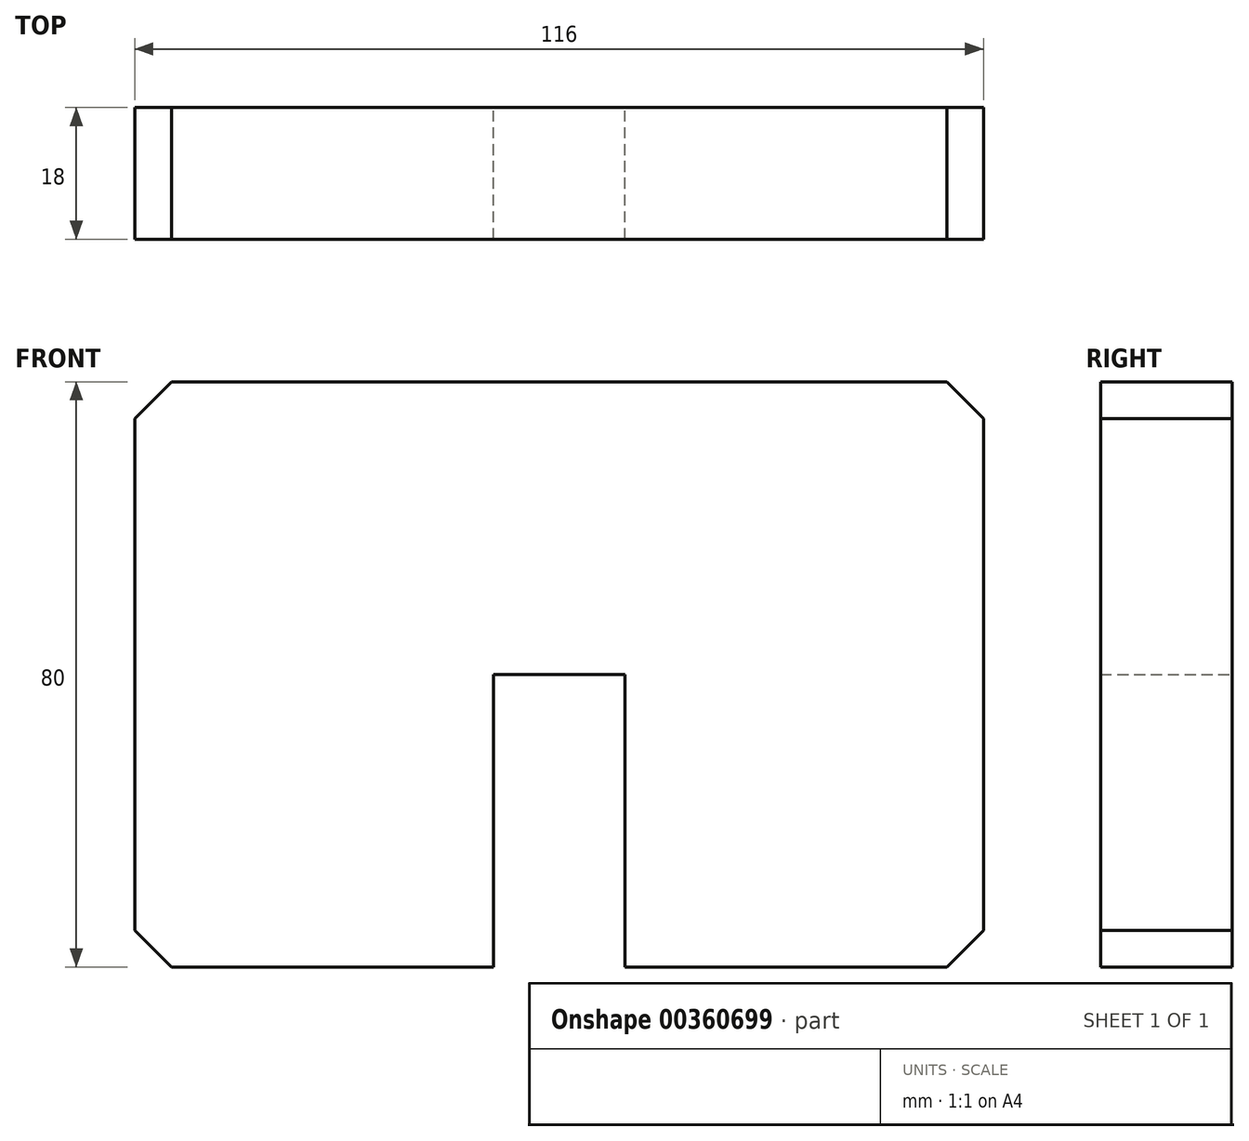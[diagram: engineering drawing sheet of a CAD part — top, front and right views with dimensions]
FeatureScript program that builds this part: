
annotation { "Feature Type Name" : "Feature", "Feature Type Description" : "" }
export const myFeature = defineFeature(function(context is Context, id is Id, definition is map)
    precondition{}
    {
        {
            var Q0;
            Q0=qCreatedBy(makeId("Front.planeOp"),FACE);
            var sketch = newSketch(context, id + "F0", { "sketchPlane" : qUnion([Q0])});
            skLineSegment(sketch, "E0.bottom", {"start": v(-58, 0) * mm, "end": v(-9, 0) * mm});
            skLineSegment(sketch, "E0.top", {"start": v(-58, 80) * mm, "end": v(58, 80) * mm});
            skLineSegment(sketch, "E0.left", {"start": v(-58, 0) * mm, "end": v(-58, 80) * mm});
            skLineSegment(sketch, "E0.right", {"start": v(58, 0) * mm, "end": v(58, 80) * mm});
            skLineSegment(sketch, "E1.top", {"start": v(-9, 40) * mm, "end": v(9, 40) * mm});
            skLineSegment(sketch, "E1.left", {"start": v(-9, 0) * mm, "end": v(-9, 40) * mm});
            skLineSegment(sketch, "E1.right", {"start": v(9, 0) * mm, "end": v(9, 40) * mm});
            skLineSegment(sketch, "E2.trimOffspring", {"start": v(9, 0) * mm, "end": v(58, 0) * mm});
            skSolve(sketch);
        }
        {
            var Q0;
            Q0=makeQuery(id+"F0.imprint","IMPRINT",FACE,{"disambiguationData":[TD([[makeQuery(id+"F0.imprint","IMPRINT",EDGE,{"derivedFrom":sQuery(id+"F0.wireOp",EDGE,"E0.bottom")}),1.0]])]});
            extrude(context, id + "F1", {"entities" : qUnion([Q0]), "depth" : 18 * mm});
        }
        {
            var Q0;
            Q0=makeQuery(id+"F1.opExtrude","SWEPT_EDGE",EDGE,{"disambiguationData":[OSD([sQuery(id+"F0.wireOp",EDGE,"E0.top"),sQuery(id+"F0.wireOp",EDGE,"E0.left")])]});
            var Q1;
            Q1=makeQuery(id+"F1.opExtrude","SWEPT_EDGE",EDGE,{"disambiguationData":[OSD([sQuery(id+"F0.wireOp",EDGE,"E0.bottom"),sQuery(id+"F0.wireOp",EDGE,"E0.left")])]});
            var Q2;
            Q2=makeQuery(id+"F1.opExtrude","SWEPT_EDGE",EDGE,{"disambiguationData":[OSD([sQuery(id+"F0.wireOp",EDGE,"E0.top"),sQuery(id+"F0.wireOp",EDGE,"E0.right")])]});
            var Q3;
            Q3=makeQuery(id+"F1.opExtrude","SWEPT_EDGE",EDGE,{"disambiguationData":[OSD([sQuery(id+"F0.wireOp",EDGE,"E0.right"),sQuery(id+"F0.wireOp",EDGE,"E2.trimOffspring")])]});
            chamfer(context, id + "F2", {"entities" : qUnion([Q0, Q1, Q2, Q3]), "width" : 5 * mm, "tangentPropagation" : true});
        }
    });
